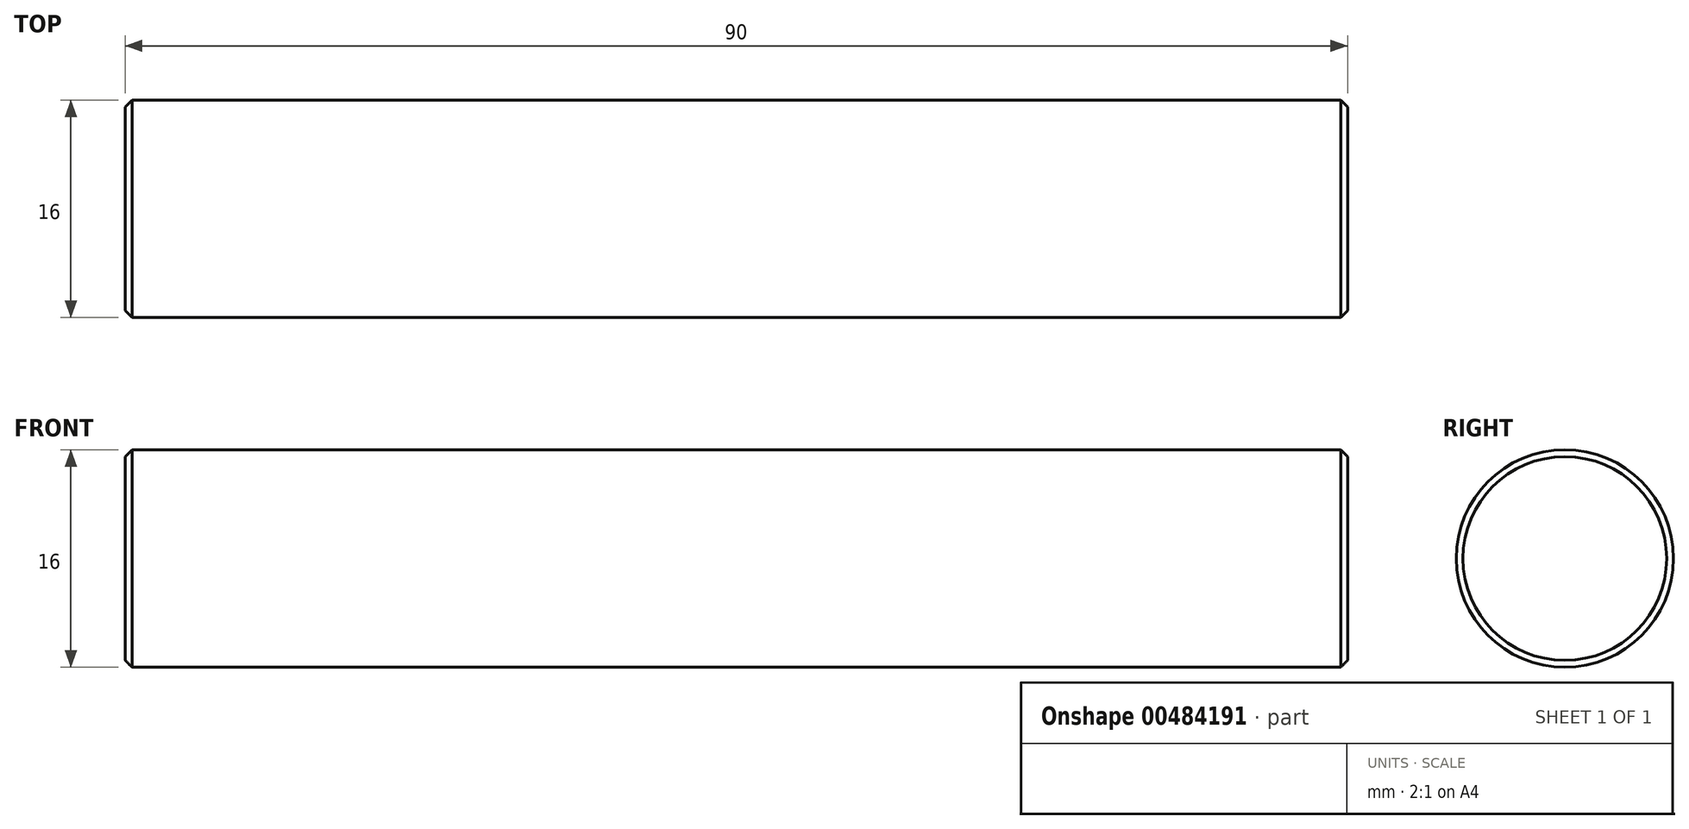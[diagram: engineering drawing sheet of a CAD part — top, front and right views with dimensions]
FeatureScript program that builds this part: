
annotation { "Feature Type Name" : "Feature", "Feature Type Description" : "" }
export const myFeature = defineFeature(function(context is Context, id is Id, definition is map)
    precondition{}
    {
        {
            var Q0;
            Q0=qCreatedBy(makeId("Top.planeOp"),FACE);
            var sketch = newSketch(context, id + "F0", { "sketchPlane" : qUnion([Q0])});
            skLineSegment(sketch, "E0.bottom", {"start": v(0, 0) * mm, "end": v(-90, 0) * mm});
            skLineSegment(sketch, "E0.top", {"start": v(0, 8) * mm, "end": v(-90, 8) * mm});
            skLineSegment(sketch, "E0.left", {"start": v(0, 0) * mm, "end": v(0, 8) * mm});
            skLineSegment(sketch, "E0.right", {"start": v(-90, 0) * mm, "end": v(-90, 8) * mm});
            skSolve(sketch);
        }
        {
            var Q0;
            Q0 = qSketchRegion(id + "F0", true);
            var Q1;
            Q1=sQuery(id+"F0.wireOp",EDGE,"E0.bottom");
            revolve(context, id + "F1", {"surfaceOperationType" : NewSurfaceOperationType.NEW, "entities" : qUnion([Q0]), "axis" : qUnion([Q1]), "revolveType" : RevolveType.FULL});
        }
        {
            var Q0;
            Q0=makeQuery(id+"F1.opRevolve","SWEPT_EDGE",EDGE,{"disambiguationData":[OSD([sQuery(id+"F0.wireOp",EDGE,"E0.top"),sQuery(id+"F0.wireOp",EDGE,"E0.right")])]});
            var Q1;
            Q1=makeQuery(id+"F1.opRevolve","SWEPT_EDGE",EDGE,{"disambiguationData":[OSD([sQuery(id+"F0.wireOp",EDGE,"E0.top"),sQuery(id+"F0.wireOp",EDGE,"E0.left")])]});
            chamfer(context, id + "F2", {"entities" : qUnion([Q0, Q1]), "width" : 0.5 * mm, "tangentPropagation" : true});
        }
    });
